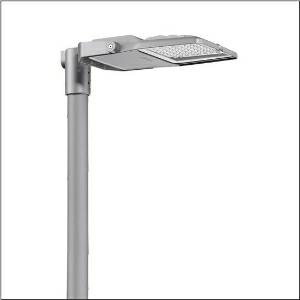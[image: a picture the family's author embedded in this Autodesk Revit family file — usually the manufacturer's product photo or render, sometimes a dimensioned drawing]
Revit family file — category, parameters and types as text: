
# Revit family: floodlight_fl_21_iq_mini___pl43_5xa7772c2a3a_c494
name_source: partatom
category: Lighting Fixtures
units: mm (PartAtom-declared; Revit-internal decimal feet)

## family parameters
Cut with Voids When Loaded = No
Host = Face
Light Source = No
Part Type = Normal
Room Calculation Point = No
Round Connector Dimension = Use Diameter
Shared = No

## types (1)
- --- (1 x LED, 12520 lm, 87.2 W, 3000K)
    Apparent Load = 87 VA
    CIE Flux Codes = 27 78 99 100 100
    Color Rendering = 70
    Color Temperature = 3000K
    Default Elevation = 1800 mm
    Description = Floodlight FL 21 iQ mini, floodlight, primary light control with lens, of PMMA, primary optical cover: protective disc, of toughened safety glass, transparent, light distribution: PL43, light emission: direct distribution, installation type: surface-mounted, LED, High Power LED, rated luminous flux: 12.520lm, luminous efficacy: 144lm/W, light colour: 730, colour temperature: 3000K, control gear: iQ Street-Remote/DALI, control: Auto-Match, Temp-Guard, Night-Set, Smart-Wire, Desk-Remote (wireless, voltage-free reading and setting of iQ features in the workshop via application-optimized NFC function/RFID function), optimised constant luminous flux control (CLO 2.0), Light-Fading, Lumen-Switch, with terminal, 6-pole, mains connection: 220..240V, AC, 50/60Hz, start of lifetime: 87W, end of service life: 92W, reduction: 40W, luminaire housing, of diecast aluminium, powder-coated, Siteco® metallic grey (DB 702S), corrosivity category C5 mid according to DIN EN ISO 12944, suitable for swimming pools, chlorine-resistant, sealing non-destructively replaceable, please order mast flange separately, mast bracket, of steel, galvanised, powder-coated, protection rating (complete): IP66, insulation class (complete): insulation class II (safety insulation), certification: CE, ENEC, VDE, protection symbol: D, impact resistance: IK08, permissible operating ambient temperature: -40..+40°C, permissible operating ambient temperature for outdoor applications: -40..+50°C, standard: DIN EN 12944, LABS conformity tested according to VDMA 24364:2018-05, packaging unit: 1 piece

Light Distribution: PL43
    Height = 70 mm
    Lamp = 1 x LED
    Lamp Light Flux = 12520 lm
    Lamp Power = 87.2 W
    Lamp count = 1
    Length = 485 mm
    Luminous efficacy = 144 lm/W
    Manufacturer = Siteco
    ModVariant = No
    Model = 5XA7772C2A3A
    Number of Poles = 1
    OnlyDefault = Yes
    Power Factor = 1
    Product Name = Floodlight FL 21 iQ mini | PL43
    Product group = floodlight | pylon annexe
    ProductGroupID = 6201
    Protection Class = Protection class II
    Protection Degree = IP 66
    RLX_Detail_Level = 1
    RLX_Emergency_Light_Flux = 0 lm
    RLX_Emergency_Type = 0
    RLX_Emergency_Type_DB = No
    RlxData = <blob elided: 101325 chars, md5=a3480214>
    Socket = socket
    Standby Power = 0 W
    System Light Flux = 12520 lm
    System Power = 87 W
    Type Comments = factory setting: luminous flux: 100 % | dim-lin: 254 | 456 mA
    Type Image = l_1007125.jpg
    URL = http://relux.com
    VarID = @adj_183755
    Voltage = 0 V
    Weight = 0.00 kg
    Width = 337 mm

## geometry (parser evidence)
native form markers: Blend x4, Sweep x13
no freeform markers — native parametric forms only
